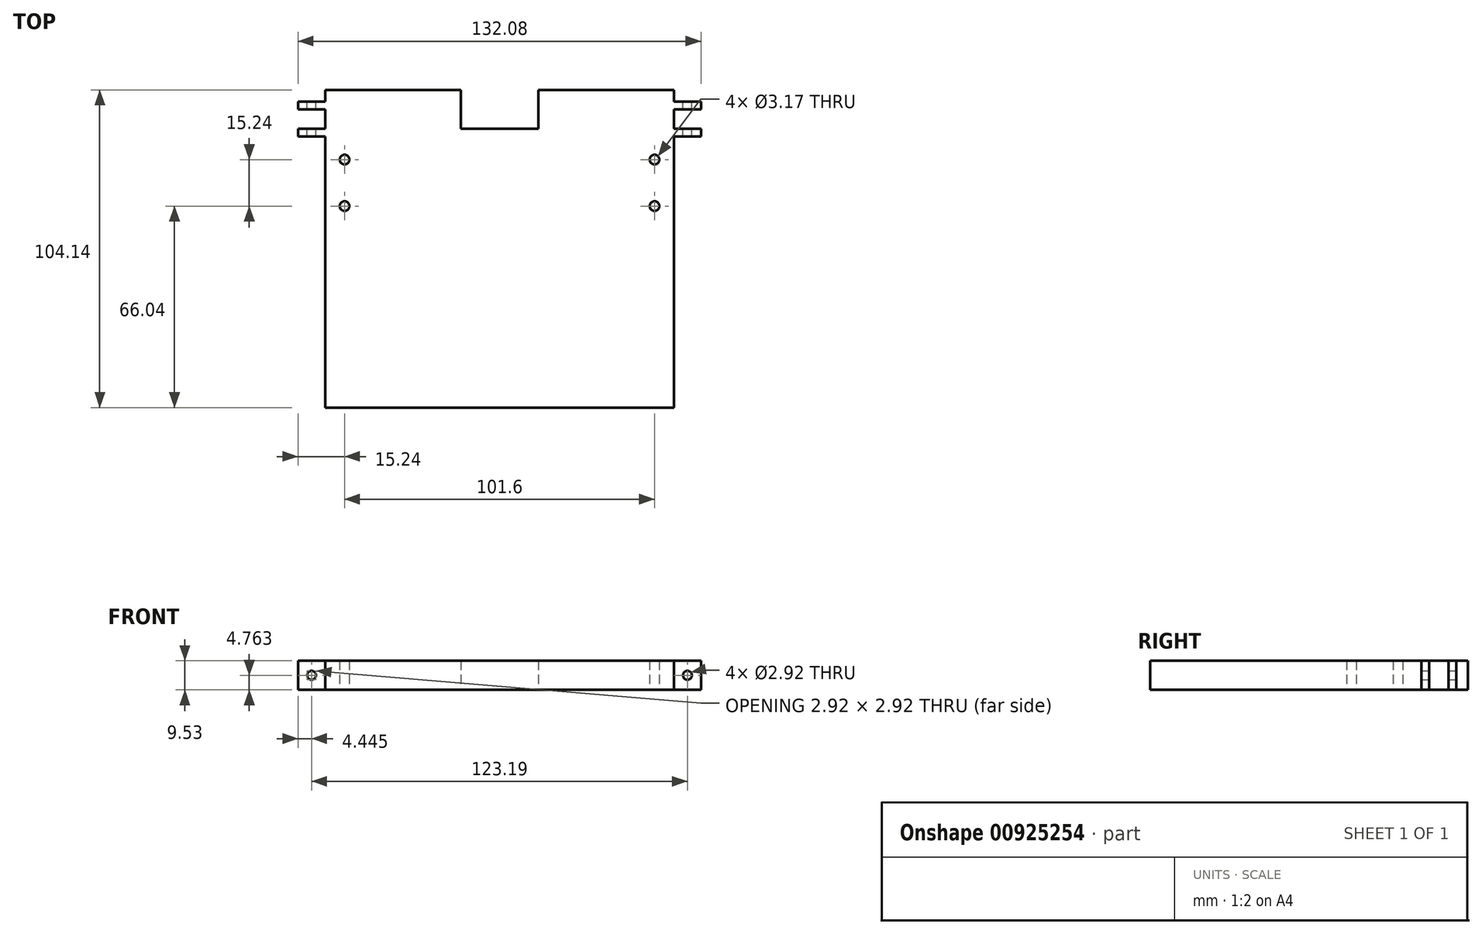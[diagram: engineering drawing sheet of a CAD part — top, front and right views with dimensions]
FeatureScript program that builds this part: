
annotation { "Feature Type Name" : "Feature", "Feature Type Description" : "" }
export const myFeature = defineFeature(function(context is Context, id is Id, definition is map)
    precondition{}
    {
        {
            var Q0;
            Q0=qCreatedBy(makeId("Top.planeOp"),FACE);
            var sketch = newSketch(context, id + "F0", { "sketchPlane" : qUnion([Q0])});
            skLineSegment(sketch, "E0.bottom", {"start": v(57.15, 104.14) * mm, "end": v(12.7, 104.14) * mm});
            skLineSegment(sketch, "E0.left", {"start": v(57.15, 104.14) * mm, "end": v(57.15, 100.33) * mm});
            skPoint(sketch, "E0.middle", {"position": v(0, 0) * mm});
            skLineSegment(sketch, "E1", {"start": v(0, 0) * mm, "end": v(0, 199.35) * mm, "construction": true});
            skLineSegment(sketch, "E2", {"start": v(57.15, 94.61) * mm, "end": v(78.58, 94.61) * mm, "construction": true});
            skLineSegment(sketch, "E3", {"start": v(57.15, 97.8) * mm, "end": v(66.04, 97.8) * mm});
            skLineSegment(sketch, "E4", {"start": v(66.04, 97.79) * mm, "end": v(66.04, 100.33) * mm});
            skLineSegment(sketch, "E5", {"start": v(66.04, 100.33) * mm, "end": v(57.15, 100.33) * mm});
            skLineSegment(sketch, "E6.MirrorCS", {"start": v(57.15, 91.44) * mm, "end": v(66.04, 91.44) * mm});
            skLineSegment(sketch, "E7.MirrorCS", {"start": v(66.04, 91.44) * mm, "end": v(66.04, 88.9) * mm});
            skLineSegment(sketch, "E8.MirrorCS", {"start": v(66.04, 88.9) * mm, "end": v(57.15, 88.9) * mm});
            skLineSegment(sketch, "E9", {"start": v(0, 0) * mm, "end": v(202.61, 0) * mm, "construction": true});
            skLineSegment(sketch, "E10.trimOffspring", {"start": v(57.15, 97.8) * mm, "end": v(57.15, 91.44) * mm});
            skLineSegment(sketch, "E11", {"start": v(57.15, 0) * mm, "end": v(0, 0) * mm});
            skLineSegment(sketch, "E12.MirrorCS", {"start": v(0, 0) * mm, "end": v(0, -199.35) * mm, "construction": true});
            skLineSegment(sketch, "E13.MirrorCS", {"start": v(-57.15, 0) * mm, "end": v(0, 0) * mm});
            skLineSegment(sketch, "E14", {"start": v(57.15, 88.9) * mm, "end": v(57.15, 0) * mm});
            skLineSegment(sketch, "E15.MirrorCS", {"start": v(-66.04, 97.79) * mm, "end": v(-66.04, 100.33) * mm});
            skLineSegment(sketch, "E16.MirrorCS", {"start": v(-66.04, 91.44) * mm, "end": v(-66.04, 88.9) * mm});
            skLineSegment(sketch, "E17.MirrorCS", {"start": v(-57.15, 104.14) * mm, "end": v(-57.15, 100.33) * mm});
            skLineSegment(sketch, "E18.MirrorCS", {"start": v(-57.15, 97.8) * mm, "end": v(-57.15, 91.44) * mm});
            skLineSegment(sketch, "E19.MirrorCS", {"start": v(-57.15, 91.44) * mm, "end": v(-66.04, 91.44) * mm});
            skLineSegment(sketch, "E20.MirrorCS", {"start": v(-57.15, 104.14) * mm, "end": v(-12.7, 104.14) * mm});
            skLineSegment(sketch, "E21.MirrorCS", {"start": v(-66.04, 88.9) * mm, "end": v(-57.15, 88.9) * mm});
            skLineSegment(sketch, "E22.MirrorCS", {"start": v(-57.15, 97.79) * mm, "end": v(-66.04, 97.79) * mm});
            skLineSegment(sketch, "E23.MirrorCS", {"start": v(-57.15, 88.9) * mm, "end": v(-57.15, 0) * mm});
            skLineSegment(sketch, "E24.MirrorCS", {"start": v(-66.04, 100.33) * mm, "end": v(-57.15, 100.33) * mm});
            skLineSegment(sketch, "E25", {"start": v(0, 91.44) * mm, "end": v(12.7, 91.44) * mm});
            skLineSegment(sketch, "E26", {"start": v(12.7, 91.44) * mm, "end": v(12.7, 104.14) * mm});
            skLineSegment(sketch, "E27.MirrorCS", {"start": v(-12.7, 91.44) * mm, "end": v(-12.7, 104.14) * mm});
            skLineSegment(sketch, "E28.MirrorCS", {"start": v(0, 91.44) * mm, "end": v(-12.7, 91.44) * mm});
            skPoint(sketch, "E29.orphan", {"position": v(0, 104.14) * mm});
            skSolve(sketch);
        }
        {
            var Q0;
            Q0 = qSketchRegion(id + "F0", true);
            extrude(context, id + "F1", {"entities" : qUnion([Q0]), "depth" : 9.52 * mm, "offsetDistance" : 25.4 * mm});
        }
        {
            var Q0;
            Q0=makeQuery(id+"F1.opExtrude","SWEPT_FACE",FACE,{"disambiguationData":[OSD([sQuery(id+"F0.wireOp",EDGE,"E5")])]});
            var sketch = newSketch(context, id + "F2", { "sketchPlane" : qUnion([Q0])});
            skLineSegment(sketch, "E30", {"start": v(0, 0) * mm, "end": v(0, 31.95) * mm, "construction": true});
            skLineSegment(sketch, "E31", {"start": v(-66.04, 4.76) * mm, "end": v(-57.15, 4.76) * mm, "construction": true});
            skCircle(sketch, "E32", {"center": v(-61.6, 4.76) * mm, "radius": 1.46 * mm});
            skCircle(sketch, "E33.MirrorC", {"center": v(61.6, 4.76) * mm, "radius": 1.46 * mm});
            skSolve(sketch);
        }
        {
            var Q0;
            Q0 = qSketchRegion(id + "F2", true);
            extrude(context, id + "F3", {"entities" : qUnion([Q0]), "operationType" : NewBodyOperationType.REMOVE, "endBound" : BoundingType.THROUGH_ALL, "oppositeDirection" : true, "depth" : 25.4 * mm, "offsetDistance" : 25.4 * mm});
        }
        {
            var Q0;
            Q0=makeQuery(id+"F1.opExtrude","CAP_FACE",FACE,{"disambiguationData":[OSD([sQuery(id+"F0.wireOp",EDGE,"E0.bottom"),sQuery(id+"F0.wireOp",EDGE,"E0.left"),sQuery(id+"F0.wireOp",EDGE,"E3"),sQuery(id+"F0.wireOp",EDGE,"E4"),sQuery(id+"F0.wireOp",EDGE,"E5"),sQuery(id+"F0.wireOp",EDGE,"E6.MirrorCS"),sQuery(id+"F0.wireOp",EDGE,"E7.MirrorCS"),sQuery(id+"F0.wireOp",EDGE,"E8.MirrorCS"),sQuery(id+"F0.wireOp",EDGE,"E10.trimOffspring"),sQuery(id+"F0.wireOp",EDGE,"E11"),sQuery(id+"F0.wireOp",EDGE,"E13.MirrorCS"),sQuery(id+"F0.wireOp",EDGE,"E14"),sQuery(id+"F0.wireOp",EDGE,"E15.MirrorCS"),sQuery(id+"F0.wireOp",EDGE,"E16.MirrorCS"),sQuery(id+"F0.wireOp",EDGE,"E17.MirrorCS"),sQuery(id+"F0.wireOp",EDGE,"E18.MirrorCS"),sQuery(id+"F0.wireOp",EDGE,"E19.MirrorCS"),sQuery(id+"F0.wireOp",EDGE,"E20.MirrorCS"),sQuery(id+"F0.wireOp",EDGE,"E21.MirrorCS"),sQuery(id+"F0.wireOp",EDGE,"E22.MirrorCS"),sQuery(id+"F0.wireOp",EDGE,"E23.MirrorCS"),sQuery(id+"F0.wireOp",EDGE,"E24.MirrorCS")])],"isStart":true});
            var sketch = newSketch(context, id + "F4", { "sketchPlane" : qUnion([Q0])});
            skLineSegment(sketch, "E34", {"start": v(0, 0) * mm, "end": v(0, -129.58) * mm, "construction": true});
            skCircle(sketch, "E35", {"center": v(50.8, -81.28) * mm, "radius": 1.59 * mm});
            skCircle(sketch, "E36", {"center": v(50.8, -66.04) * mm, "radius": 1.59 * mm});
            skCircle(sketch, "E37.MirrorC", {"center": v(-50.8, -81.28) * mm, "radius": 1.59 * mm});
            skCircle(sketch, "E38.MirrorC", {"center": v(-50.8, -66.04) * mm, "radius": 1.59 * mm});
            skSolve(sketch);
        }
        {
            var Q0;
            Q0 = qSketchRegion(id + "F4", true);
            extrude(context, id + "F5", {"entities" : qUnion([Q0]), "operationType" : NewBodyOperationType.REMOVE, "endBound" : BoundingType.THROUGH_ALL, "oppositeDirection" : true, "depth" : 25.4 * mm, "offsetDistance" : 25.4 * mm});
        }
    });
